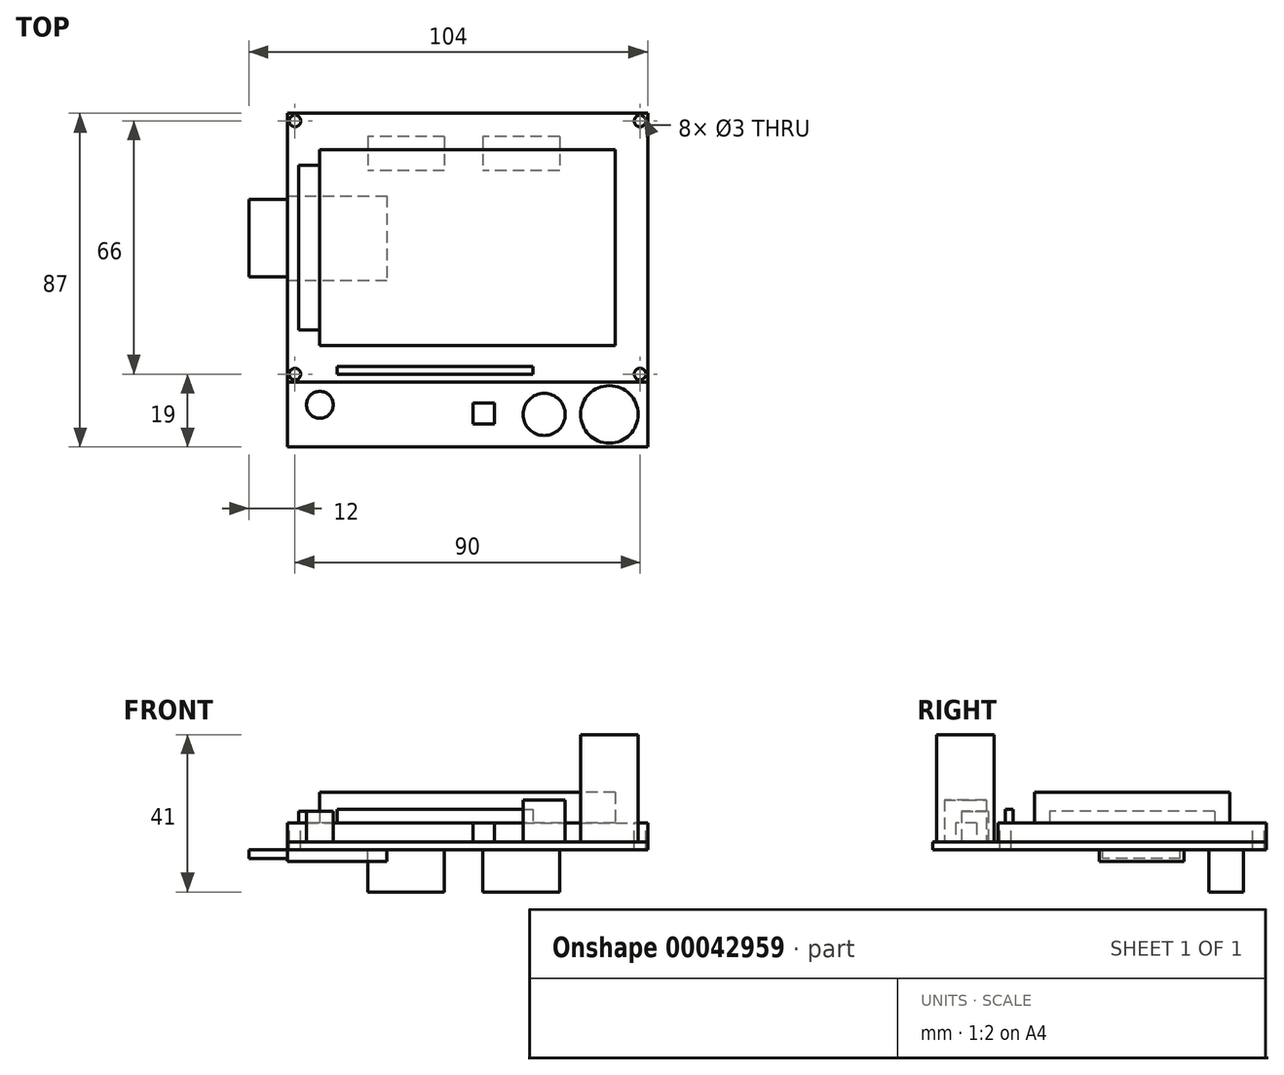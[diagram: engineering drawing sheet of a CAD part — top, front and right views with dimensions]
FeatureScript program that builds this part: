
annotation { "Feature Type Name" : "Feature", "Feature Type Description" : "" }
export const myFeature = defineFeature(function(context is Context, id is Id, definition is map)
    precondition{}
    {
        {
            var Q0;
            Q0=qCreatedBy(makeId("Top.planeOp"),FACE);
            var sketch = newSketch(context, id + "F0", { "sketchPlane" : qUnion([Q0])});
            skLineSegment(sketch, "E0.rect.bottom", {"start": v(47, 43.5) * mm, "end": v(-47, 43.5) * mm});
            skLineSegment(sketch, "E0.rect.top", {"start": v(47, -43.5) * mm, "end": v(-47, -43.5) * mm});
            skLineSegment(sketch, "E0.rect.left", {"start": v(47, 43.5) * mm, "end": v(47, -43.5) * mm});
            skLineSegment(sketch, "E0.rect.right", {"start": v(-47, 43.5) * mm, "end": v(-47, -43.5) * mm});
            skPoint(sketch, "E0.rect.middle", {"position": v(0, 0) * mm});
            skSolve(sketch);
        }
        {
            var Q0;
            Q0=makeQuery(id+"F0.imprint","IMPRINT",FACE,{"disambiguationData":[TD([[makeQuery(id+"F0.imprint","IMPRINT",EDGE,{"derivedFrom":sQuery(id+"F0.wireOp",EDGE,"E0.rect.bottom")}),1.0]])]});
            extrude(context, id + "F1", {"entities" : qUnion([Q0]), "depth" : 2 * mm});
        }
        {
            var Q0;
            Q0=makeQuery(id+"F1.opExtrude","CAP_FACE",FACE,{"disambiguationData":[OSD([sQuery(id+"F0.wireOp",EDGE,"E0.rect.bottom"),sQuery(id+"F0.wireOp",EDGE,"E0.rect.top"),sQuery(id+"F0.wireOp",EDGE,"E0.rect.left"),sQuery(id+"F0.wireOp",EDGE,"E0.rect.right")])],"isStart":false});
            var sketch = newSketch(context, id + "F2", { "sketchPlane" : qUnion([Q0])});
            skLineSegment(sketch, "E1.bottom", {"start": v(-47, 43.5) * mm, "end": v(47, 43.5) * mm});
            skLineSegment(sketch, "E1.top", {"start": v(-47, -26.5) * mm, "end": v(47, -26.5) * mm});
            skLineSegment(sketch, "E1.left", {"start": v(-47, 43.5) * mm, "end": v(-47, -26.5) * mm});
            skLineSegment(sketch, "E1.right", {"start": v(47, 43.5) * mm, "end": v(47, -26.5) * mm});
            skSolve(sketch);
        }
        {
            var Q0;
            Q0=makeQuery(id+"F2.imprint","IMPRINT",FACE,{"disambiguationData":[TD([[makeQuery(id+"F2.imprint","IMPRINT",EDGE,{"derivedFrom":sQuery(id+"F2.wireOp",EDGE,"E1.bottom")}),1.0]])]});
            extrude(context, id + "F3", {"entities" : qUnion([Q0]), "depth" : 5 * mm});
        }
        {
            var Q0;
            Q0=makeQuery(id+"F3.opExtrude","CAP_FACE",FACE,{"disambiguationData":[OSD([sQuery(id+"F2.wireOp",EDGE,"E1.bottom"),sQuery(id+"F2.wireOp",EDGE,"E1.top"),sQuery(id+"F2.wireOp",EDGE,"E1.left"),sQuery(id+"F2.wireOp",EDGE,"E1.right")])],"isStart":false});
            var sketch = newSketch(context, id + "F4", { "sketchPlane" : qUnion([Q0])});
            skLineSegment(sketch, "E2.rect.bottom", {"start": v(38.5, 34) * mm, "end": v(-38.5, 34) * mm});
            skLineSegment(sketch, "E2.rect.top", {"start": v(38.5, -17) * mm, "end": v(-38.5, -17) * mm});
            skLineSegment(sketch, "E2.rect.left", {"start": v(38.5, 34) * mm, "end": v(38.5, -17) * mm});
            skLineSegment(sketch, "E2.rect.right", {"start": v(-38.5, 34) * mm, "end": v(-38.5, -17) * mm});
            skPoint(sketch, "E2.rect.middle", {"position": v(0, 8.5) * mm});
            skSolve(sketch);
        }
        {
            var Q0;
            Q0=makeQuery(id+"F4.imprint","IMPRINT",FACE,{"disambiguationData":[TD([[makeQuery(id+"F4.imprint","IMPRINT",EDGE,{"derivedFrom":sQuery(id+"F4.wireOp",EDGE,"E2.rect.bottom")}),1.0]])]});
            extrude(context, id + "F5", {"entities" : qUnion([Q0]), "depth" : 8 * mm});
        }
        {
            var Q0;
            Q0=makeQuery(id+"F3.opExtrude","CAP_FACE",FACE,{"disambiguationData":[OSD([sQuery(id+"F2.wireOp",EDGE,"E1.bottom"),sQuery(id+"F2.wireOp",EDGE,"E1.top"),sQuery(id+"F2.wireOp",EDGE,"E1.left"),sQuery(id+"F2.wireOp",EDGE,"E1.right")])],"isStart":false});
            var sketch = newSketch(context, id + "F6", { "sketchPlane" : qUnion([Q0])});
            skLineSegment(sketch, "E3.bottom", {"start": v(-38.5, 30) * mm, "end": v(-44, 30) * mm});
            skLineSegment(sketch, "E3.top", {"start": v(-38.5, -13) * mm, "end": v(-44, -13) * mm});
            skLineSegment(sketch, "E3.left", {"start": v(-38.5, 30) * mm, "end": v(-38.5, -13) * mm});
            skLineSegment(sketch, "E3.right", {"start": v(-44, 30) * mm, "end": v(-44, -13) * mm});
            skSolve(sketch);
        }
        {
            var Q0;
            Q0=makeQuery(id+"F6.imprint","IMPRINT",FACE,{"disambiguationData":[TD([[makeQuery(id+"F6.imprint","IMPRINT",EDGE,{"derivedFrom":sQuery(id+"F6.wireOp",EDGE,"E3.bottom")}),1.0]])]});
            extrude(context, id + "F7", {"entities" : qUnion([Q0]), "depth" : 3 * mm});
        }
        {
            var Q0;
            Q0=makeQuery(id+"F1.opExtrude","CAP_FACE",FACE,{"disambiguationData":[OSD([sQuery(id+"F0.wireOp",EDGE,"E0.rect.bottom"),sQuery(id+"F0.wireOp",EDGE,"E0.rect.top"),sQuery(id+"F0.wireOp",EDGE,"E0.rect.left"),sQuery(id+"F0.wireOp",EDGE,"E0.rect.right")])],"isStart":false});
            var sketch = newSketch(context, id + "F8", { "sketchPlane" : qUnion([Q0])});
            skCircle(sketch, "E4", {"center": v(37, -35) * mm, "radius": 7.5 * mm});
            skSolve(sketch);
        }
        {
            var Q0;
            Q0=makeQuery(id+"F8.imprint","IMPRINT",FACE,{"disambiguationData":[TD([[makeQuery(id+"F8.imprint","IMPRINT",EDGE,{"derivedFrom":sQuery(id+"F8.wireOp",EDGE,"E4")}),1.0]])]});
            extrude(context, id + "F9", {"entities" : qUnion([Q0]), "depth" : 28 * mm});
        }
        {
            var Q0;
            Q0=makeQuery(id+"F1.opExtrude","CAP_FACE",FACE,{"disambiguationData":[OSD([sQuery(id+"F0.wireOp",EDGE,"E0.rect.bottom"),sQuery(id+"F0.wireOp",EDGE,"E0.rect.top"),sQuery(id+"F0.wireOp",EDGE,"E0.rect.left"),sQuery(id+"F0.wireOp",EDGE,"E0.rect.right")])],"isStart":false});
            var sketch = newSketch(context, id + "F10", { "sketchPlane" : qUnion([Q0])});
            skCircle(sketch, "E5", {"center": v(20, -35) * mm, "radius": 5.5 * mm});
            skSolve(sketch);
        }
        {
            var Q0;
            Q0=makeQuery(id+"F10.imprint","IMPRINT",FACE,{"disambiguationData":[TD([[makeQuery(id+"F10.imprint","IMPRINT",EDGE,{"derivedFrom":sQuery(id+"F10.wireOp",EDGE,"E5")}),1.0]])]});
            extrude(context, id + "F11", {"entities" : qUnion([Q0]), "depth" : 11 * mm});
        }
        {
            var Q0;
            Q0=makeQuery(id+"F1.opExtrude","CAP_FACE",FACE,{"disambiguationData":[OSD([sQuery(id+"F0.wireOp",EDGE,"E0.rect.bottom"),sQuery(id+"F0.wireOp",EDGE,"E0.rect.top"),sQuery(id+"F0.wireOp",EDGE,"E0.rect.left"),sQuery(id+"F0.wireOp",EDGE,"E0.rect.right")])],"isStart":false});
            var sketch = newSketch(context, id + "F12", { "sketchPlane" : qUnion([Q0])});
            skLineSegment(sketch, "E6.bottom", {"start": v(7, -32) * mm, "end": v(1.5, -32) * mm});
            skLineSegment(sketch, "E6.top", {"start": v(7, -37.5) * mm, "end": v(1.5, -37.5) * mm});
            skLineSegment(sketch, "E6.left", {"start": v(7, -32) * mm, "end": v(7, -37.5) * mm});
            skLineSegment(sketch, "E6.right", {"start": v(1.5, -32) * mm, "end": v(1.5, -37.5) * mm});
            skSolve(sketch);
        }
        {
            var Q0;
            Q0=makeQuery(id+"F12.imprint","IMPRINT",FACE,{"disambiguationData":[TD([[makeQuery(id+"F12.imprint","IMPRINT",EDGE,{"derivedFrom":sQuery(id+"F12.wireOp",EDGE,"E6.bottom")}),1.0]])]});
            extrude(context, id + "F13", {"entities" : qUnion([Q0]), "depth" : 5 * mm});
        }
        {
            var Q0;
            Q0=makeQuery(id+"F1.opExtrude","CAP_FACE",FACE,{"disambiguationData":[OSD([sQuery(id+"F0.wireOp",EDGE,"E0.rect.bottom"),sQuery(id+"F0.wireOp",EDGE,"E0.rect.top"),sQuery(id+"F0.wireOp",EDGE,"E0.rect.left"),sQuery(id+"F0.wireOp",EDGE,"E0.rect.right")])],"isStart":false});
            var sketch = newSketch(context, id + "F14", { "sketchPlane" : qUnion([Q0])});
            skCircle(sketch, "E7", {"center": v(-38.5, -32.5) * mm, "radius": 3.5 * mm});
            skSolve(sketch);
        }
        {
            var Q0;
            Q0=makeQuery(id+"F14.imprint","IMPRINT",FACE,{"disambiguationData":[TD([[makeQuery(id+"F14.imprint","IMPRINT",EDGE,{"derivedFrom":sQuery(id+"F14.wireOp",EDGE,"E7")}),1.0]])]});
            extrude(context, id + "F15", {"entities" : qUnion([Q0]), "depth" : 8 * mm});
        }
        {
            var Q0;
            Q0=makeQuery(id+"F3.opExtrude","CAP_FACE",FACE,{"disambiguationData":[OSD([sQuery(id+"F2.wireOp",EDGE,"E1.bottom"),sQuery(id+"F2.wireOp",EDGE,"E1.top"),sQuery(id+"F2.wireOp",EDGE,"E1.left"),sQuery(id+"F2.wireOp",EDGE,"E1.right")])],"isStart":false});
            var sketch = newSketch(context, id + "F16", { "sketchPlane" : qUnion([Q0])});
            skPoint(sketch, "E8", {"position": v(-45, 41.5) * mm});
            skPoint(sketch, "E9.MirrorP", {"position": v(45, 41.5) * mm});
            skPoint(sketch, "E10", {"position": v(45, -24.5) * mm});
            skPoint(sketch, "E11", {"position": v(-45, -24.5) * mm});
            skSolve(sketch);
        }
        {
            var Q0;
            Q0=sQuery(id+"F16.wireOp",VERTEX,"E8");
            var Q1;
            Q1=makeQuery(id+"F3.opExtrude","SWEPT_BODY",BODY,{"disambiguationData":[OSD([sQuery(id+"F2.wireOp",EDGE,"E1.bottom"),sQuery(id+"F2.wireOp",EDGE,"E1.top"),sQuery(id+"F2.wireOp",EDGE,"E1.left"),sQuery(id+"F2.wireOp",EDGE,"E1.right")])]});
            var Q2;
            Q2=makeQuery(id+"F1.opExtrude","SWEPT_BODY",BODY,{"disambiguationData":[OSD([sQuery(id+"F0.wireOp",EDGE,"E0.rect.bottom"),sQuery(id+"F0.wireOp",EDGE,"E0.rect.top"),sQuery(id+"F0.wireOp",EDGE,"E0.rect.left"),sQuery(id+"F0.wireOp",EDGE,"E0.rect.right")])]});
            hole(context, id + "F17", {"style" : HoleStyle.SIMPLE, "holeDiameter" : 3 * mm, "endStyle" : HoleEndStyle.BLIND, "holeDepth" : 20 * mm, "locations" : qUnion([Q0]), "scope" : qUnion([Q1, Q2])});
        }
        {
            var Q0;
            Q0=sQuery(id+"F16.wireOp",VERTEX,"E9.MirrorP");
            var Q1;
            Q1=sQuery(id+"F16.wireOp",VERTEX,"E10");
            var Q2;
            Q2=sQuery(id+"F16.wireOp",VERTEX,"E11");
            var Q3;
            Q3=makeQuery(id+"F3.opExtrude","SWEPT_BODY",BODY,{"disambiguationData":[OSD([sQuery(id+"F2.wireOp",EDGE,"E1.bottom"),sQuery(id+"F2.wireOp",EDGE,"E1.top"),sQuery(id+"F2.wireOp",EDGE,"E1.left"),sQuery(id+"F2.wireOp",EDGE,"E1.right")])]});
            var Q4;
            Q4=makeQuery(id+"F1.opExtrude","SWEPT_BODY",BODY,{"disambiguationData":[OSD([sQuery(id+"F0.wireOp",EDGE,"E0.rect.bottom"),sQuery(id+"F0.wireOp",EDGE,"E0.rect.top"),sQuery(id+"F0.wireOp",EDGE,"E0.rect.left"),sQuery(id+"F0.wireOp",EDGE,"E0.rect.right")])]});
            hole(context, id + "F18", {"style" : HoleStyle.SIMPLE, "holeDiameter" : 3 * mm, "endStyle" : HoleEndStyle.THROUGH, "locations" : qUnion([Q0, Q1, Q2]), "scope" : qUnion([Q3, Q4])});
        }
        {
            var Q0;
            Q0=makeQuery(id+"F16.imprint","IMPRINT",FACE,{"disambiguationData":[TD([[makeQuery(id+"F16.imprint","IMPRINT",EDGE,{"derivedFrom":makeQuery(id+"F3.opExtrude","CAP_EDGE",EDGE,{"disambiguationData":[OSD([sQuery(id+"F2.wireOp",EDGE,"E1.bottom")])],"isStart":false})}),1.0]])]});
            var sketch = newSketch(context, id + "F19", { "sketchPlane" : qUnion([Q0])});
            skLineSegment(sketch, "E12.bottom", {"start": v(-34, -24.5) * mm, "end": v(17, -24.5) * mm});
            skLineSegment(sketch, "E12.top", {"start": v(-34, -22.5) * mm, "end": v(17, -22.5) * mm});
            skLineSegment(sketch, "E12.left", {"start": v(-34, -24.5) * mm, "end": v(-34, -22.5) * mm});
            skLineSegment(sketch, "E12.right", {"start": v(17, -24.5) * mm, "end": v(17, -22.5) * mm});
            skSolve(sketch);
        }
        {
            var Q0;
            Q0=makeQuery(id+"F19.imprint","IMPRINT",FACE,{"disambiguationData":[TD([[makeQuery(id+"F19.imprint","IMPRINT",EDGE,{"derivedFrom":sQuery(id+"F19.wireOp",EDGE,"E12.bottom")}),1.0]])]});
            extrude(context, id + "F20", {"entities" : qUnion([Q0]), "depth" : 3.5 * mm});
        }
        {
            var Q0;
            Q0=makeQuery(id+"F1.opExtrude","CAP_FACE",FACE,{"disambiguationData":[OSD([sQuery(id+"F0.wireOp",EDGE,"E0.rect.bottom"),sQuery(id+"F0.wireOp",EDGE,"E0.rect.top"),sQuery(id+"F0.wireOp",EDGE,"E0.rect.left"),sQuery(id+"F0.wireOp",EDGE,"E0.rect.right")])],"isStart":true});
            var sketch = newSketch(context, id + "F21", { "sketchPlane" : qUnion([Q0])});
            skLineSegment(sketch, "E13.bottom", {"start": v(-47, -22) * mm, "end": v(-21, -22) * mm});
            skLineSegment(sketch, "E13.top", {"start": v(-47, 0) * mm, "end": v(-21, 0) * mm});
            skLineSegment(sketch, "E13.left", {"start": v(-47, -22) * mm, "end": v(-47, 0) * mm});
            skLineSegment(sketch, "E13.right", {"start": v(-21, -22) * mm, "end": v(-21, 0) * mm});
            skSolve(sketch);
        }
        {
            var Q0;
            Q0=makeQuery(id+"F21.imprint","IMPRINT",FACE,{"disambiguationData":[TD([[makeQuery(id+"F21.imprint","IMPRINT",EDGE,{"derivedFrom":sQuery(id+"F21.wireOp",EDGE,"E13.bottom")}),1.0]])]});
            extrude(context, id + "F22", {"entities" : qUnion([Q0]), "operationType" : NewBodyOperationType.ADD, "depth" : 3 * mm});
        }
        {
            var Q0;
            Q0=makeQuery(id+"F1.opExtrude","CAP_FACE",FACE,{"disambiguationData":[OSD([sQuery(id+"F0.wireOp",EDGE,"E0.rect.bottom"),sQuery(id+"F0.wireOp",EDGE,"E0.rect.top"),sQuery(id+"F0.wireOp",EDGE,"E0.rect.left"),sQuery(id+"F0.wireOp",EDGE,"E0.rect.right")])],"isStart":true});
            var sketch = newSketch(context, id + "F23", { "sketchPlane" : qUnion([Q0])});
            skLineSegment(sketch, "E14.bottom", {"start": v(24, -37.5) * mm, "end": v(4, -37.5) * mm});
            skLineSegment(sketch, "E14.top", {"start": v(24, -28.5) * mm, "end": v(4, -28.5) * mm});
            skLineSegment(sketch, "E14.left", {"start": v(24, -37.5) * mm, "end": v(24, -28.5) * mm});
            skLineSegment(sketch, "E14.right", {"start": v(4, -37.5) * mm, "end": v(4, -28.5) * mm});
            skLineSegment(sketch, "E15.bottom", {"start": v(-6, -37.5) * mm, "end": v(-26, -37.5) * mm});
            skLineSegment(sketch, "E15.top", {"start": v(-6, -28.5) * mm, "end": v(-26, -28.5) * mm});
            skLineSegment(sketch, "E15.left", {"start": v(-6, -37.5) * mm, "end": v(-6, -28.5) * mm});
            skLineSegment(sketch, "E15.right", {"start": v(-26, -37.5) * mm, "end": v(-26, -28.5) * mm});
            skSolve(sketch);
        }
        {
            var Q0;
            Q0 = qSketchRegion(id + "F23", true);
            extrude(context, id + "F24", {"entities" : qUnion([Q0]), "operationType" : NewBodyOperationType.ADD, "depth" : 11 * mm});
        }
        {
            var Q0;
            Q0=makeQuery(id+"F22.boolean.opBoolean","MERGE",FACE,{"derivedFrom":[makeQuery(id+"F1.opExtrude","SWEPT_FACE",FACE,{"disambiguationData":[OSD([sQuery(id+"F0.wireOp",EDGE,"E0.rect.right")])]}),makeQuery(id+"F22.opExtrude","SWEPT_FACE",FACE,{"disambiguationData":[OSD([sQuery(id+"F21.wireOp",EDGE,"E13.left")])]})]});
            var sketch = newSketch(context, id + "F25", { "sketchPlane" : qUnion([Q0])});
            skLineSegment(sketch, "E16.bottom", {"start": v(-21.06, -2.3) * mm, "end": v(-0.87, -2.3) * mm});
            skLineSegment(sketch, "E16.top", {"start": v(-21.06, 0) * mm, "end": v(-0.87, 0) * mm});
            skLineSegment(sketch, "E16.left", {"start": v(-21.06, -2.3) * mm, "end": v(-21.06, 0) * mm});
            skLineSegment(sketch, "E16.right", {"start": v(-0.87, -2.3) * mm, "end": v(-0.87, 0) * mm});
            skSolve(sketch);
        }
        {
            var Q0;
            Q0 = qSketchRegion(id + "F25", true);
            var Q1;
            Q1=makeQuery(id+"F25.imprint","IMPRINT",FACE,{"disambiguationData":[TD([[makeQuery(id+"F25.imprint","IMPRINT",EDGE,{"derivedFrom":sQuery(id+"F25.wireOp",EDGE,"E16.bottom")}),1.0]])]});
            extrude(context, id + "F26", {"entities" : qUnion([Q0, Q1]), "operationType" : NewBodyOperationType.ADD, "depth" : 10 * mm});
        }
    });
